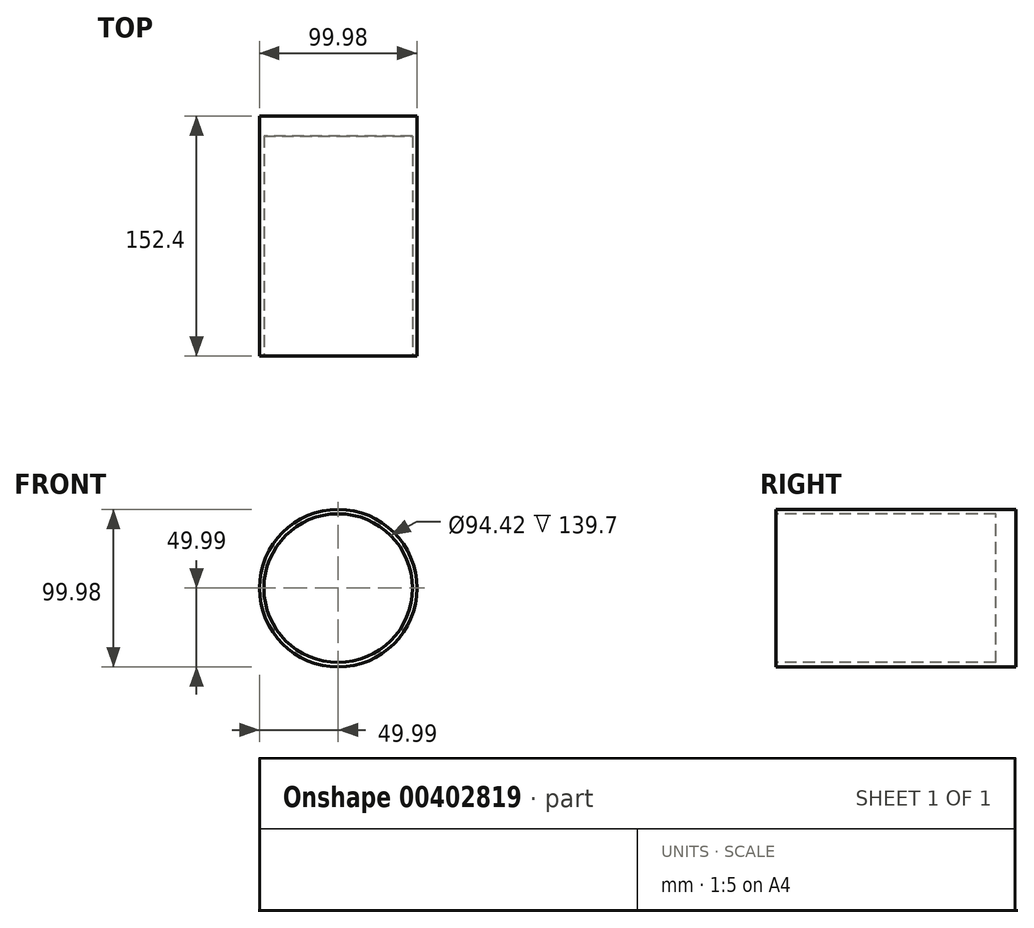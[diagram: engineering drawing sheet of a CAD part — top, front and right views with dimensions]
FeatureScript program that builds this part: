
annotation { "Feature Type Name" : "Feature", "Feature Type Description" : "" }
export const myFeature = defineFeature(function(context is Context, id is Id, definition is map)
    precondition{}
    {
        {
            var Q0;
            Q0=qCreatedBy(makeId("Front.planeOp"),FACE);
            var sketch = newSketch(context, id + "F0", { "sketchPlane" : qUnion([Q0])});
            skCircle(sketch, "E0", {"center": v(0, 0) * mm, "radius": 49.99 * mm});
            skSolve(sketch);
        }
        {
            var Q0;
            Q0 = qSketchRegion(id + "F0", true);
            extrude(context, id + "F1", {"entities" : qUnion([Q0]), "depth" : 152.4 * mm});
        }
        {
            var Q0;
            Q0=makeQuery(id+"F1.opExtrude","CAP_FACE",FACE,{"disambiguationData":[OSD([sQuery(id+"F0.wireOp",EDGE,"E0")])],"isStart":false});
            var sketch = newSketch(context, id + "F2", { "sketchPlane" : qUnion([Q0])});
            skCircle(sketch, "E1", {"center": v(0, 0) * mm, "radius": 47.2 * mm});
            skSolve(sketch);
        }
        {
            var Q0;
            Q0=makeQuery(id+"F2.imprint","IMPRINT",FACE,{"disambiguationData":[TD([[makeQuery(id+"F2.imprint","IMPRINT",EDGE,{"derivedFrom":sQuery(id+"F2.wireOp",EDGE,"E1")}),1.0]])]});
            var Q1;
            Q1=sQuery(id+"F2.wireOp",EDGE,"E1");
            extrude(context, id + "F3", {"entities" : qUnion([Q0]), "operationType" : NewBodyOperationType.REMOVE, "surfaceEntities" : qUnion([Q1]), "oppositeDirection" : true, "depth" : 139.7 * mm});
        }
    });
